# Revit family: PRD_FrankeWS_WlHngWshBsns_Heavy-DutyWashBasin_HDTX455
name_source: partatom
category: Plumbing Fixtures
revit_build: Autodesk Revit 2018 (Build: 20190510_1515(x64)
units: mm (PartAtom-declared; Revit-internal decimal feet)

## family parameters
Cut with Voids When Loaded = No
Host = Face
OmniClass Number = 23.45.05.14.14
OmniClass Title = Sinks/Lavatories
Part Type = Normal
Room Calculation Point = No
Round Connector Dimension = Use Diameter
Shared = No

## types (1)
- HDTX455
    AssetType = Fixed
    BIMObjectName = PRD_AR_WallHungWashBasins_Heavy-DutyWashBasin_HDTX455
    Category = Pr_40_20_96_96, Wall-hung wash basins
    Color = Stainless steel
    Default Elevation = 850 mm  [stored 2.78871 ft]
    Description = Wash basin for wall mounting, hidden mounting with stainless steel rods through wall, fixing and service via maintenance room, stainless steel, surface satin finished, material thickness 1.2 mm, seamless welded round bowl with diameter 347 mm, without tap ledge, without overflow, seamless welded waste with 32 mm drain pipe, drainage centric, for recessed trap mounting - trap not included, incl. stainless steel rods and nuts.
    DrainSize = DN 32 (1 1/4 inch.)
    DurationUnit = year
    Features = stainless steel, 1.20 mm, satin finished, bolt fix with duct wall, 500x160x425 mm (WxHxD)
    Finish = Satin finished
    Form = Wall hung wash basin
    GrossWeight = 11.00 kg
    IfcExportAs = IfcSanitaryTerminalType
    IfcExportType = WASHHANDBASIN
    IntegralAccessories = Waste kit included. Stainless steel rods and nuts included
    Manufacturer = KWC Group AG
    ManufacturerName = KWC Group AG
    ManufacturerURL = www.kwc.com
    Material = Stainless steel
    MaterialsBody = Stainless steel 1.4301
    MaterialsFinishAndColour = Stainless steel, satin finished
    Model = HDTX455
    ModelNumber = 2000100058
    ModelReference = HDTX455
    NBSDescription = Wall hung wash basins
    NBSReference = 45-35-70/369
    Name = HEAVY-DUTY wash basin HDTX455
    NetWeight = 10.00 kg
    NominalDepth = 160 mm  [stored 0.524934 ft]
    NominalHeight = 160 mm  [stored 0.524934 ft]
    NominalLength = 425 mm  [stored 1.39436 ft]
    NominalWidth = 500 mm  [stored 1.64042 ft]
    ProductInformation = https://pim.kwc.com
    Size = 500 x 160 x 425 mm
    URL = www.kwc.com
    Uniclass2015Code = Pr_40_20_96_96
    Uniclass2015Title = Wall-hung wash basins
    Uniclass2015Version = Products v1.5
    Version = 1
    WarrantyDurationUnit = year
    WashHandBasinMounting = WallHung
    WashHandBasinType = HandRinse
    WashbasinMaterial = PRD_AR_StainlessSteel_SatinFinished
    WasteSize = 32
    WaterSupplyOverflowAndWasteHolesOverflow = None
    WaterSupplyOverflowAndWasteHolesWaste = Center-Center
    WaterSupplyOverflowAndWasteHolesWaterSupply = No tapholes

note: [stored X ft] marks values corroborated as IEEE doubles in the binary element streams (Revit-internal decimal feet)

## geometry (parser evidence)
native form markers: Sweep x6
no freeform markers — native parametric forms only
